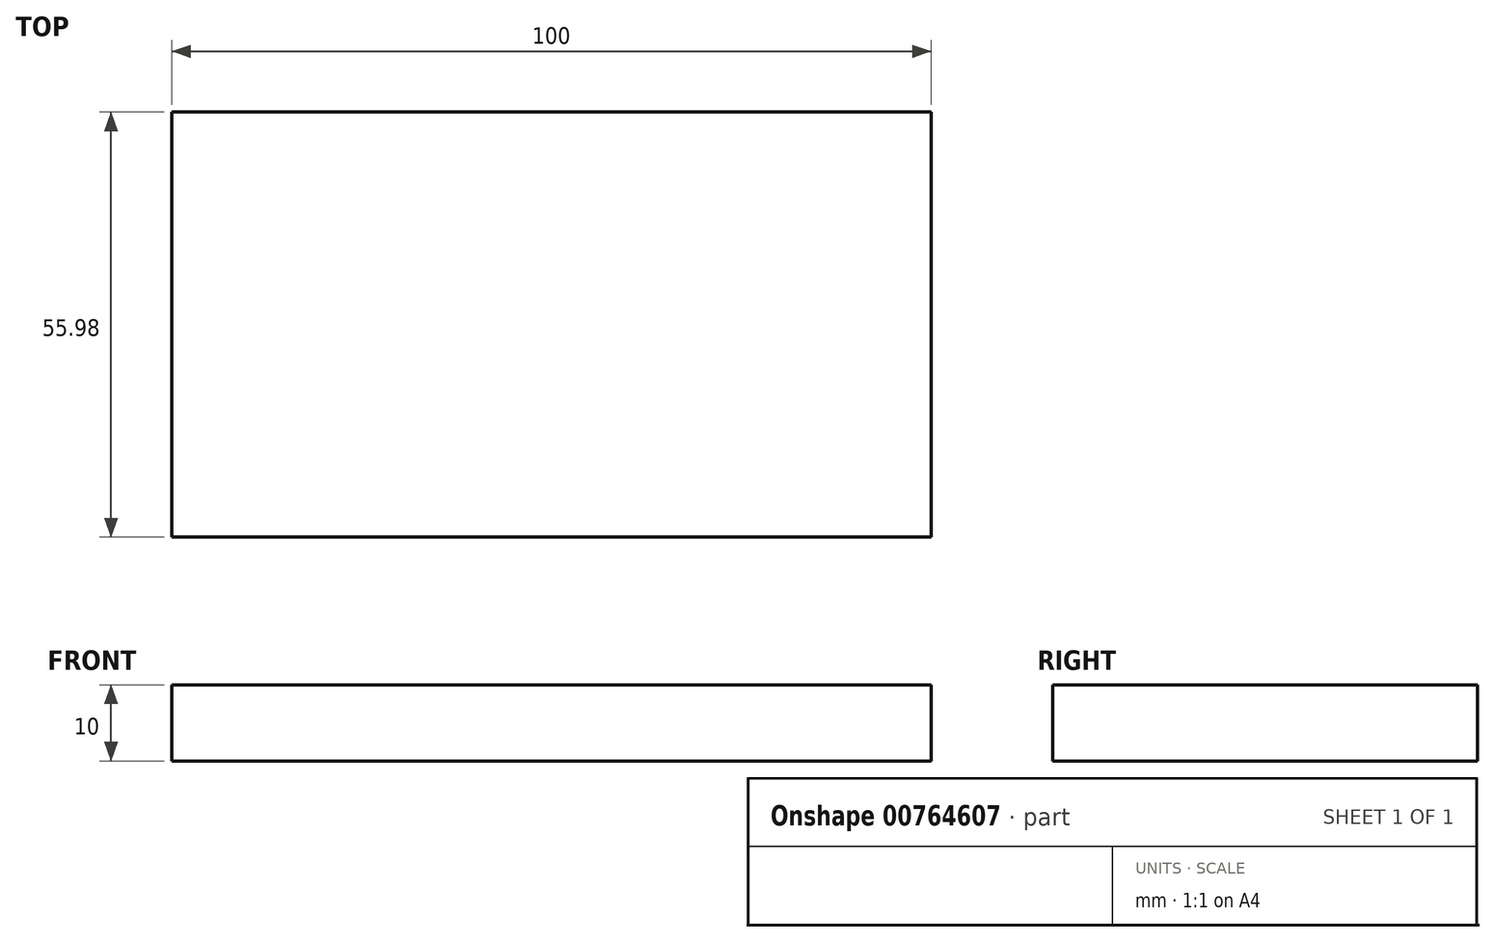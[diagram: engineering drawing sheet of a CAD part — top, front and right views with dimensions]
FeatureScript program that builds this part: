
annotation { "Feature Type Name" : "Feature", "Feature Type Description" : "" }
export const myFeature = defineFeature(function(context is Context, id is Id, definition is map)
    precondition{}
    {
        {
            var Q0;
            Q0=qCreatedBy(makeId("Top.planeOp"),FACE);
            var sketch = newSketch(context, id + "F0", { "sketchPlane" : qUnion([Q0])});
            skLineSegment(sketch, "E0.bottom", {"start": v(-53.63, -28) * mm, "end": v(46.37, -28) * mm});
            skLineSegment(sketch, "E0.top", {"start": v(-53.63, 28) * mm, "end": v(46.37, 28) * mm});
            skLineSegment(sketch, "E0.left", {"start": v(-53.63, -28) * mm, "end": v(-53.63, 28) * mm});
            skLineSegment(sketch, "E0.right", {"start": v(46.37, -28) * mm, "end": v(46.37, 28) * mm});
            skPoint(sketch, "E0.middle", {"position": v(-3.63, 0) * mm});
            skSolve(sketch);
        }
        {
            var Q0;
            Q0=makeQuery(id+"F0.imprint","IMPRINT",FACE,{"disambiguationData":[TD([[makeQuery(id+"F0.imprint","IMPRINT",EDGE,{"derivedFrom":sQuery(id+"F0.wireOp",EDGE,"E0.bottom")}),1.0]])]});
            extrude(context, id + "F1", {"entities" : qUnion([Q0]), "depth" : 10 * mm, "offsetDistance" : 25 * mm});
        }
    });
